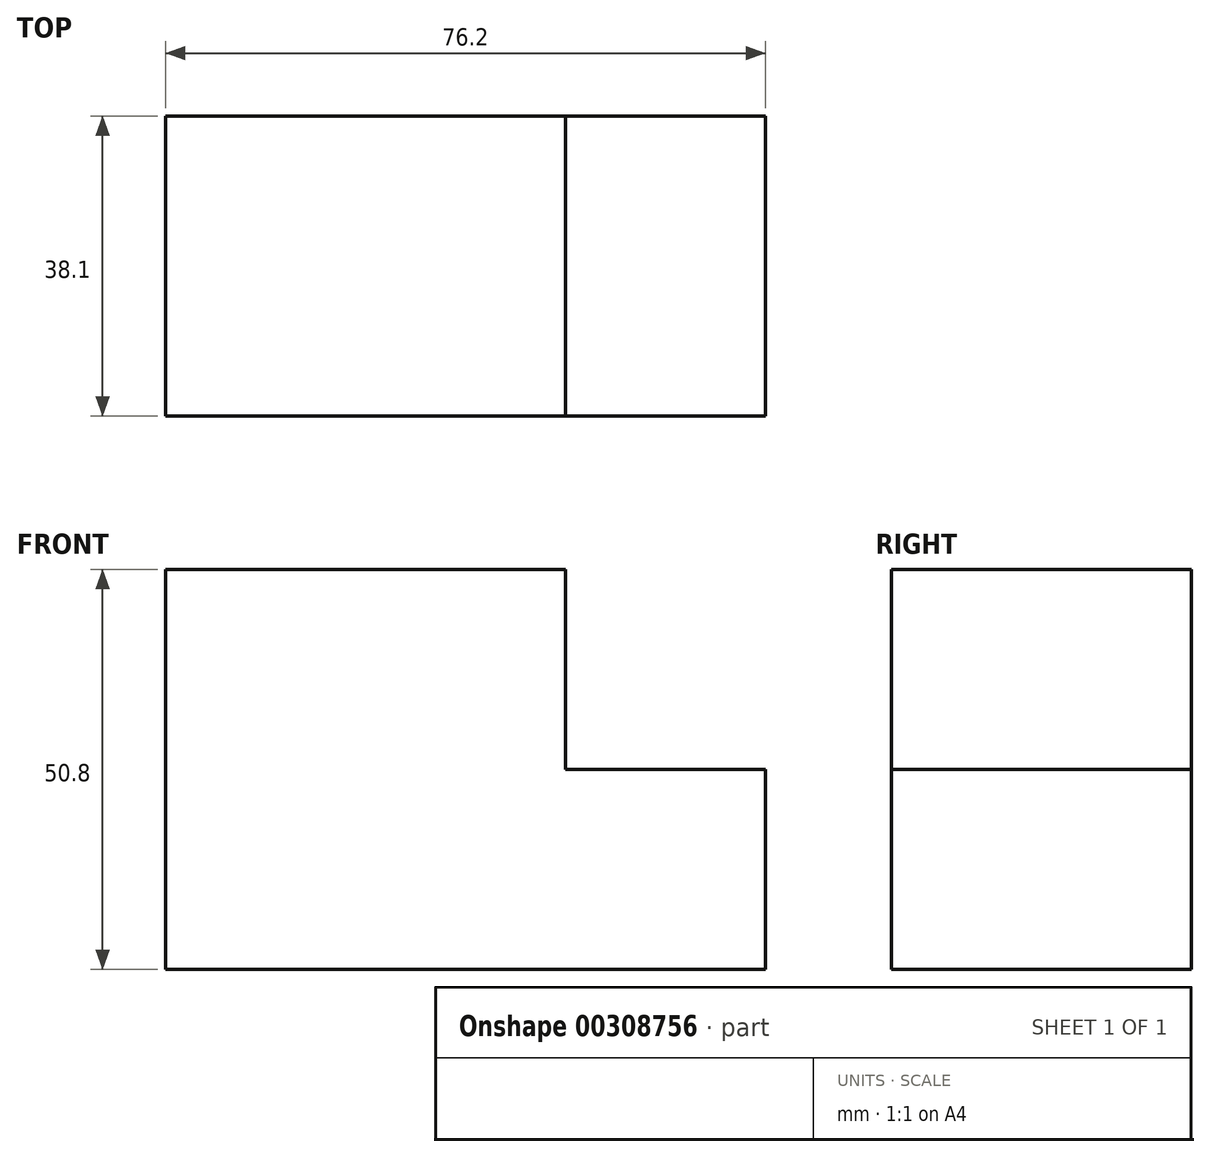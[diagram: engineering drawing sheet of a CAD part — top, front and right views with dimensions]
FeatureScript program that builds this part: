
annotation { "Feature Type Name" : "Feature", "Feature Type Description" : "" }
export const myFeature = defineFeature(function(context is Context, id is Id, definition is map)
    precondition{}
    {
        {
            var Q0;
            Q0=qCreatedBy(makeId("Front.planeOp"),FACE);
            var sketch = newSketch(context, id + "F0", { "sketchPlane" : qUnion([Q0])});
            skLineSegment(sketch, "E0", {"start": v(-40.11, -39.46) * mm, "end": v(36.09, -39.46) * mm});
            skLineSegment(sketch, "E1", {"start": v(36.09, -39.46) * mm, "end": v(36.09, -14.06) * mm});
            skLineSegment(sketch, "E2", {"start": v(36.09, -14.06) * mm, "end": v(10.69, -14.06) * mm});
            skLineSegment(sketch, "E3", {"start": v(10.69, -14.06) * mm, "end": v(10.69, 11.34) * mm});
            skLineSegment(sketch, "E4", {"start": v(10.69, 11.34) * mm, "end": v(-40.11, 11.34) * mm});
            skLineSegment(sketch, "E5", {"start": v(-40.11, 11.34) * mm, "end": v(-40.11, -39.46) * mm});
            skSolve(sketch);
        }
        {
            var Q0;
            Q0=makeQuery(id+"F0.imprint","IMPRINT",FACE,{"disambiguationData":[TD([[makeQuery(id+"F0.imprint","IMPRINT",EDGE,{"derivedFrom":sQuery(id+"F0.wireOp",EDGE,"E0")}),1.0]])]});
            extrude(context, id + "F1", {"entities" : qUnion([Q0]), "depth" : 38.1 * mm});
        }
    });
